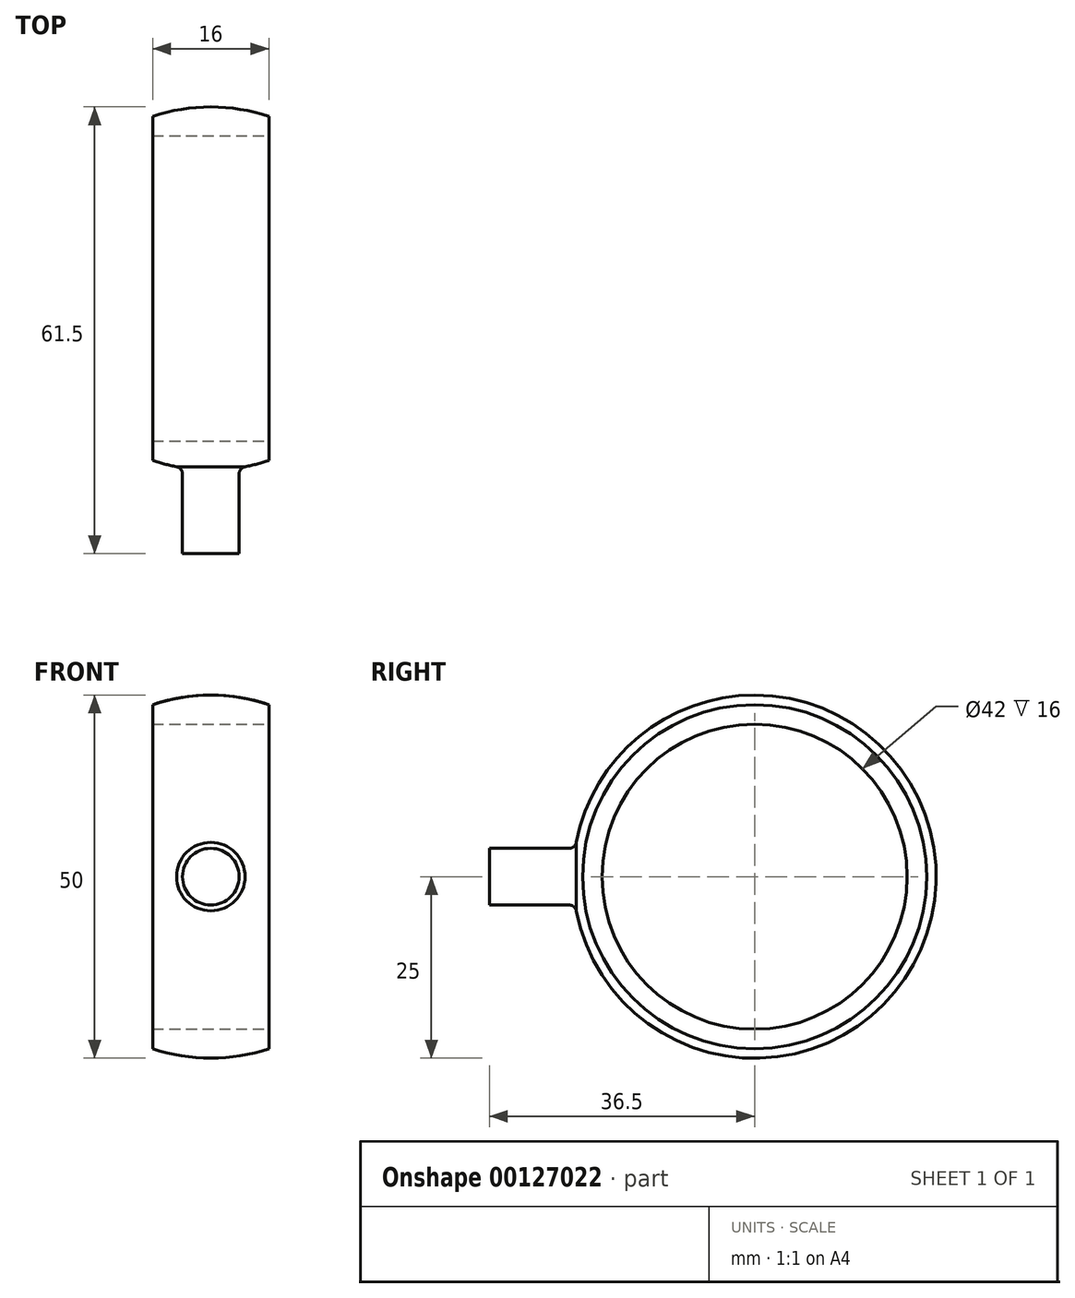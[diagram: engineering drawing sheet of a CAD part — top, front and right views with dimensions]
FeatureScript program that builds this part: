
annotation { "Feature Type Name" : "Feature", "Feature Type Description" : "" }
export const myFeature = defineFeature(function(context is Context, id is Id, definition is map)
    precondition{}
    {
        {
            var Q0;
            Q0=qCreatedBy(makeId("Front.planeOp"),FACE);
            var sketch = newSketch(context, id + "F0", { "sketchPlane" : qUnion([Q0])});
            skCircle(sketch, "E0", {"center": v(0, 0) * mm, "radius": 21 * mm});
            skCircle(sketch, "E1", {"center": v(0, 0) * mm, "radius": 25 * mm});
            skLineSegment(sketch, "E2", {"start": v(-25, 0) * mm, "end": v(25, 0) * mm});
            skSolve(sketch);
        }
        {
            var Q0;
            {var subQ0=sQuery(id+"F0.wireOp",EDGE,"E2");var subQ1=sQuery(id+"F0.wireOp",EDGE,"E0");var subQ2=makeQuery(id+"F0.imprint","INTERSECT",VERTEX,{"disambiguationData":[OD(0.0)],"derivedFrom":[subQ1,subQ0]});Q0=makeQuery(id+"F0.imprint","IMPRINT",FACE,{"disambiguationData":[TD([[makeQuery(id+"F0.imprint","IMPRINT",EDGE,{"disambiguationData":[TD([[subQ2,1.0]])],"derivedFrom":subQ1}),-1.0]])]});}
            var Q1;
            Q1=sQuery(id+"F0.wireOp",EDGE,"E2");
            revolve(context, id + "F1", {"entities" : qUnion([Q0]), "axis" : qUnion([Q1]), "revolveType" : RevolveType.FULL});
        }
        {
            var Q0;
            Q0=qCreatedBy(makeId("Front.planeOp"),FACE);
            var sketch = newSketch(context, id + "F2", { "sketchPlane" : qUnion([Q0])});
            skLineSegment(sketch, "E3.bottom", {"start": v(8, 43.57) * mm, "end": v(29.7, 43.57) * mm});
            skLineSegment(sketch, "E3.top", {"start": v(8, -44.34) * mm, "end": v(29.7, -44.34) * mm});
            skLineSegment(sketch, "E3.left", {"start": v(8, 43.57) * mm, "end": v(8, -44.34) * mm});
            skLineSegment(sketch, "E3.right", {"start": v(29.7, 43.57) * mm, "end": v(29.7, -44.34) * mm});
            skLineSegment(sketch, "E4.bottom", {"start": v(-8, 44.67) * mm, "end": v(-32.28, 44.67) * mm});
            skLineSegment(sketch, "E4.top", {"start": v(-8, -49.49) * mm, "end": v(-32.28, -49.49) * mm});
            skLineSegment(sketch, "E4.left", {"start": v(-8, 44.67) * mm, "end": v(-8, -49.49) * mm});
            skLineSegment(sketch, "E4.right", {"start": v(-32.28, 44.67) * mm, "end": v(-32.28, -49.49) * mm});
            skSolve(sketch);
        }
        {
            var Q0;
            Q0=qSketchRegion(id+"F2",true);
            extrude(context, id + "F3", {"entities" : qUnion([Q0]), "operationType" : NewBodyOperationType.REMOVE, "endBound" : BoundingType.SYMMETRIC, "oppositeDirection" : true, "depth" : 60 * mm});
        }
        {
            var Q0;
            Q0=makeQuery(id+"F3.boolean.opBoolean","COPY",FACE,{"derivedFrom":makeQuery(id+"F3.opExtrude","SWEPT_FACE",FACE,{"disambiguationData":[OSD([sQuery(id+"F2.wireOp",EDGE,"E3.left")])]})});
            var sketch = newSketch(context, id + "F4", { "sketchPlane" : qUnion([Q0])});
            skCircle(sketch, "E5", {"center": v(0, 0) * mm, "radius": 20 * mm});
            skSolve(sketch);
        }
        {
            var Q0;
            Q0=qSketchRegion(id+"F4",true);
            extrude(context, id + "F5", {"entities" : qUnion([Q0]), "operationType" : NewBodyOperationType.REMOVE, "oppositeDirection" : true, "depth" : 15 * mm});
        }
        {
            var Q0;
            Q0=makeQuery(id+"F3.boolean.opBoolean","COPY",FACE,{"derivedFrom":makeQuery(id+"F3.opExtrude","SWEPT_FACE",FACE,{"disambiguationData":[OSD([sQuery(id+"F2.wireOp",EDGE,"E3.left")])]})});
            var sketch = newSketch(context, id + "F6", { "sketchPlane" : qUnion([Q0])});
            skCircle(sketch, "E6", {"center": v(0, 0) * mm, "radius": 21 * mm});
            skSolve(sketch);
        }
        {
            var Q0;
            Q0=qSketchRegion(id+"F6",true);
            extrude(context, id + "F7", {"entities" : qUnion([Q0]), "operationType" : NewBodyOperationType.REMOVE, "endBound" : BoundingType.SYMMETRIC, "oppositeDirection" : true, "depth" : 60 * mm});
        }
        {
            var Q0;
            Q0=qCreatedBy(makeId("Front.planeOp"),FACE);
            cPlane(context, id + "F8", {"entities" : qUnion([Q0]), "cplaneType" : CPlaneType.OFFSET, "offset" : 25 * mm, "width" : 150 * mm, "height" : 150 * mm});
        }
        {
            var Q0;
            Q0=qCreatedBy(id+"F8.planeOp",FACE);
            var sketch = newSketch(context, id + "F9", { "sketchPlane" : qUnion([Q0])});
            skCircle(sketch, "E7", {"center": v(0, 0) * mm, "radius": 3.9 * mm});
            skSolve(sketch);
        }
        {
            var Q0;
            Q0=qSketchRegion(id+"F9",true);
            extrude(context, id + "F10", {"entities" : qUnion([Q0]), "endBound" : BoundingType.SYMMETRIC, "depth" : 3 * mm});
        }
        {
            var Q0;
            Q0=makeQuery(id+"F10.opExtrude","CAP_FACE",FACE,{"disambiguationData":[OSD([sQuery(id+"F9.wireOp",EDGE,"E7")])],"isStart":false});
            extrude(context, id + "F11", {"entities" : qUnion([Q0]), "operationType" : NewBodyOperationType.ADD, "depth" : 10 * mm});
        }
        {
            var Q0;
            Q0=makeQuery(id+"F10.opExtrude","SWEPT_BODY",BODY,{"disambiguationData":[OSD([sQuery(id+"F9.wireOp",EDGE,"E7")])]});
            var Q1;
            Q1=makeQuery(id+"F1.opRevolve","SWEPT_BODY",BODY,{"disambiguationData":[OSD([sQuery(id+"F0.wireOp",EDGE,"E0"),sQuery(id+"F0.wireOp",EDGE,"E1"),sQuery(id+"F0.wireOp",EDGE,"E2")])]});
            booleanBodies(context, id + "F12", {"operationType" : BooleanOperationType.UNION, "tools" : qUnion([Q0, Q1])});
        }
        {
            var Q0;
            {var subQ0=sQuery(id+"F9.wireOp",EDGE,"E7");Q0=makeQuery(id+"F12.opBoolean","INTERSECT",EDGE,{"derivedFrom":[makeQuery(id+"F1.opRevolve","SWEPT_FACE",FACE,{"disambiguationData":[OSD([sQuery(id+"F0.wireOp",EDGE,"E1")])]}),makeQuery(id+"F11.boolean.opBoolean","MERGE",FACE,{"derivedFrom":[makeQuery(id+"F10.opExtrude","SWEPT_FACE",FACE,{"disambiguationData":[OSD([subQ0])]}),makeQuery(id+"F11.opExtrude","SWEPT_FACE",FACE,{"disambiguationData":[OSD([subQ0])]})]})]});}
            fillet(context, id + "F13", {"entities" : qUnion([Q0]), "radius" : 1 * mm, "tangentPropagation" : true, "allowEdgeOverflow" : false});
        }
    });
